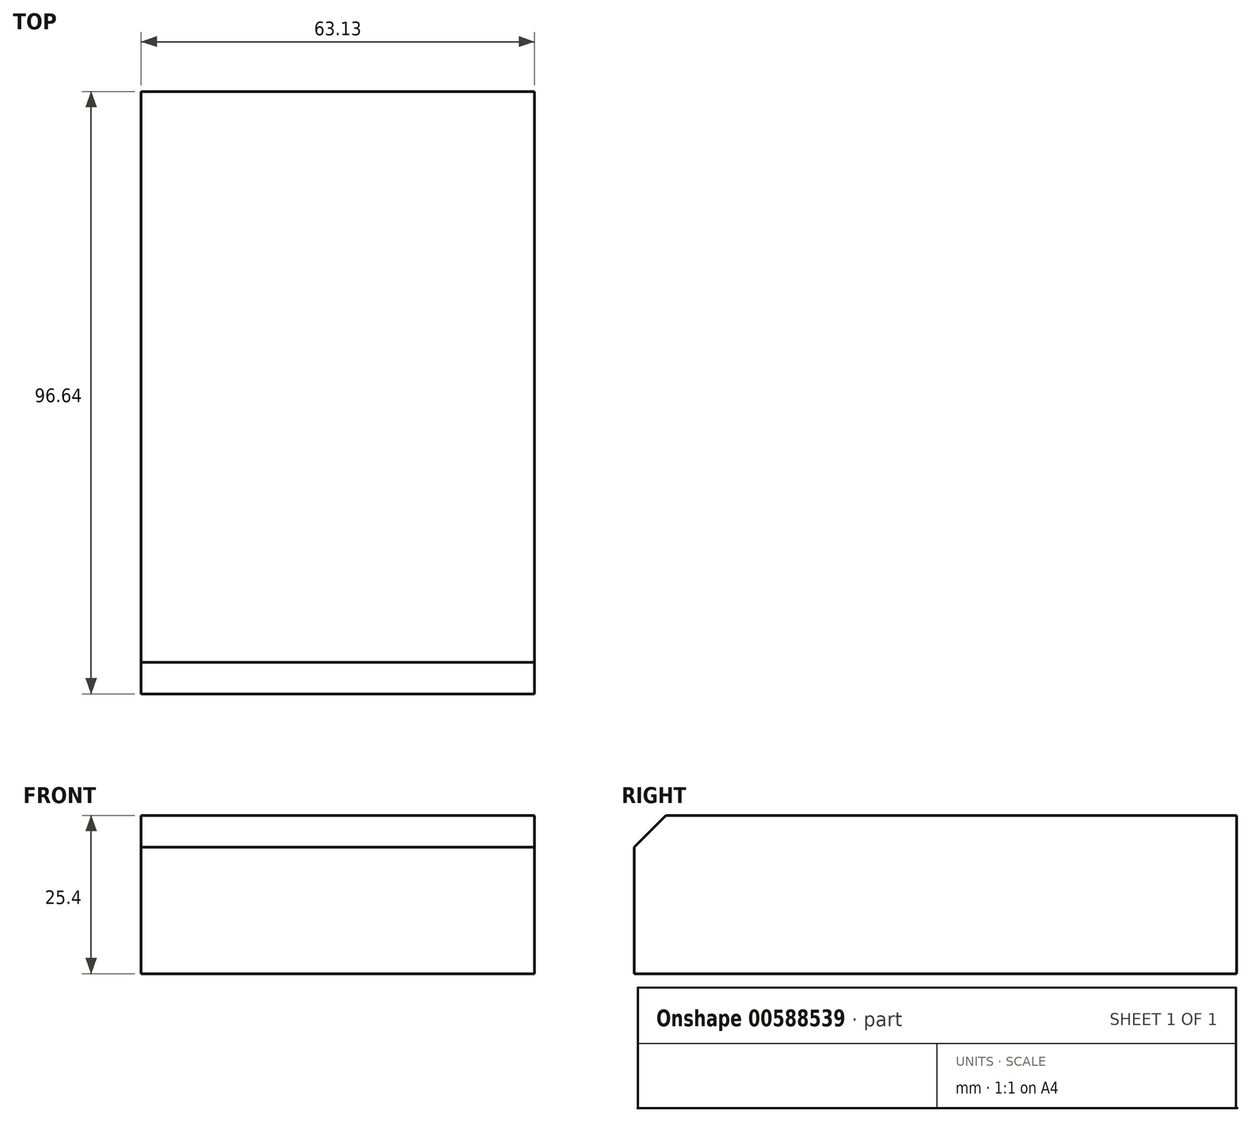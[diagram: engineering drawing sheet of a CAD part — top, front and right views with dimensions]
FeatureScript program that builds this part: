
annotation { "Feature Type Name" : "Feature", "Feature Type Description" : "" }
export const myFeature = defineFeature(function(context is Context, id is Id, definition is map)
    precondition{}
    {
        {
            var Q0;
            Q0=qCreatedBy(makeId("Top.planeOp"),FACE);
            var sketch = newSketch(context, id + "F0", { "sketchPlane" : qUnion([Q0])});
            skLineSegment(sketch, "E0.bottom", {"start": v(-63.13, 48.32) * mm, "end": v(63.13, 48.32) * mm});
            skLineSegment(sketch, "E0.top", {"start": v(-63.13, -48.32) * mm, "end": v(63.13, -48.32) * mm});
            skLineSegment(sketch, "E0.left", {"start": v(-63.13, 48.32) * mm, "end": v(-63.13, -48.32) * mm});
            skLineSegment(sketch, "E0.right", {"start": v(63.13, 48.32) * mm, "end": v(63.13, -48.32) * mm});
            skLineSegment(sketch, "E1", {"start": v(0, 48.32) * mm, "end": v(0, -48.32) * mm});
            skSolve(sketch);
        }
        {
            var Q0;
            {var subQ0=sQuery(id+"F0.wireOp",EDGE,"E0.left");Q0=makeQuery(id+"F0.imprint","IMPRINT",FACE,{"disambiguationData":[TD([[makeQuery(id+"F0.imprint","IMPRINT",EDGE,{"derivedFrom":subQ0}),1.0]])]});}
            extrude(context, id + "F1", {"entities" : qUnion([Q0]), "depth" : 25.4 * mm, "offsetDistance" : 25.4 * mm});
        }
        {
            var Q0;
            Q0=makeQuery(id+"F1.opExtrude","CAP_EDGE",EDGE,{"disambiguationData":[OSD([sQuery(id+"F0.wireOp",EDGE,"E0.top")])],"isStart":false});
            chamfer(context, id + "F2", {"entities" : qUnion([Q0]), "width" : 5.08 * mm, "tangentPropagation" : true});
        }
    });
